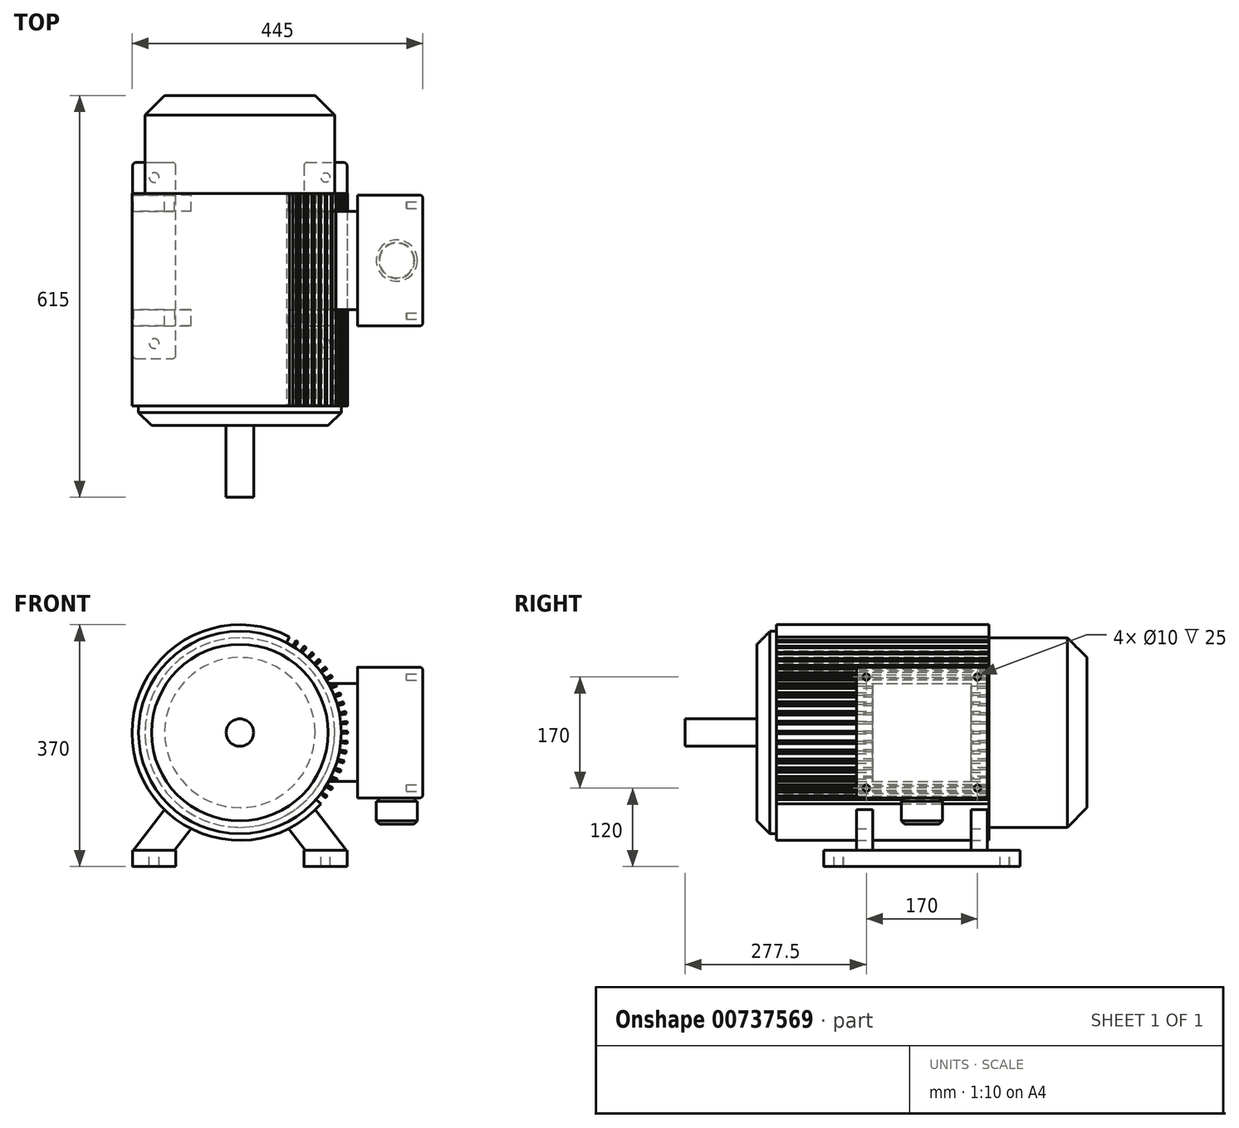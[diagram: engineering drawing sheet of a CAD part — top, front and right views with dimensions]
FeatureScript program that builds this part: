
annotation { "Feature Type Name" : "Feature", "Feature Type Description" : "" }
export const myFeature = defineFeature(function(context is Context, id is Id, definition is map)
    precondition{}
    {
        {
            var Q0;
            Q0=qCreatedBy(makeId("Front.planeOp"),FACE);
            var sketch = newSketch(context, id + "F0", { "sketchPlane" : qUnion([Q0])});
            skCircle(sketch, "E0", {"center": v(0, 0) * mm, "radius": 165 * mm});
            skSolve(sketch);
        }
        {
            var Q0;
            Q0=makeQuery(id+"F0.imprint","IMPRINT",FACE,{"disambiguationData":[TD([[makeQuery(id+"F0.imprint","IMPRINT",EDGE,{"derivedFrom":sQuery(id+"F0.wireOp",EDGE,"E0")}),1.0]])]});
            extrude(context, id + "F1", {"entities" : qUnion([Q0]), "endBound" : BoundingType.SYMMETRIC, "depth" : 505 * mm, "offsetDistance" : 25 * mm});
        }
        {
            var Q0;
            Q0=qCreatedBy(makeId("Right.planeOp"),FACE);
            var sketch = newSketch(context, id + "F2", { "sketchPlane" : qUnion([Q0])});
            skLineSegment(sketch, "E1", {"start": v(-447.5, 165) * mm, "end": v(252.5, 165) * mm});
            skLineSegment(sketch, "E2", {"start": v(252.5, 165) * mm, "end": v(252.5, 115) * mm});
            skLineSegment(sketch, "E3", {"start": v(252.5, 115) * mm, "end": v(202.5, 165) * mm});
            skSolve(sketch);
        }
        {
            var Q0;
            Q0 = qSketchRegion(id + "F2", true);
            var Q1;
            Q1=makeQuery(id+"F1.opExtrude","SWEPT_FACE",FACE,{"disambiguationData":[OSD([sQuery(id+"F0.wireOp",EDGE,"E0")])]});
            revolve(context, id + "F3", {"operationType" : NewBodyOperationType.REMOVE, "surfaceOperationType" : NewSurfaceOperationType.NEW, "entities" : qUnion([Q0]), "axis" : qUnion([Q1]), "revolveType" : RevolveType.FULL, "oppositeDirection" : true});
        }
        {
            var Q0;
            Q0=qCreatedBy(makeId("Right.planeOp"),FACE);
            var sketch = newSketch(context, id + "F4", { "sketchPlane" : qUnion([Q0])});
            skLineSegment(sketch, "E4", {"start": v(-447.5, 165) * mm, "end": v(377.5, 165) * mm});
            skLineSegment(sketch, "E5.bottom", {"start": v(102.5, 165) * mm, "end": v(232.5, 165) * mm});
            skLineSegment(sketch, "E5.top", {"start": v(102.5, 145) * mm, "end": v(232.5, 145) * mm});
            skLineSegment(sketch, "E5.left", {"start": v(102.5, 165) * mm, "end": v(102.5, 145) * mm});
            skLineSegment(sketch, "E5.right", {"start": v(232.5, 165) * mm, "end": v(232.5, 145) * mm});
            skSolve(sketch);
        }
        {
            var Q0;
            Q0 = qSketchRegion(id + "F4", true);
            var Q1;
            Q1=makeQuery(id+"F1.opExtrude","SWEPT_FACE",FACE,{"disambiguationData":[OSD([sQuery(id+"F0.wireOp",EDGE,"E0")])]});
            revolve(context, id + "F5", {"operationType" : NewBodyOperationType.REMOVE, "surfaceOperationType" : NewSurfaceOperationType.NEW, "entities" : qUnion([Q0]), "axis" : qUnion([Q1]), "revolveType" : RevolveType.FULL, "oppositeDirection" : true});
        }
        {
            var Q0;
            Q0=qCreatedBy(makeId("Right.planeOp"),FACE);
            var sketch = newSketch(context, id + "F6", { "sketchPlane" : qUnion([Q0])});
            skLineSegment(sketch, "E6", {"start": v(-447.5, 165) * mm, "end": v(-252.5, 165) * mm});
            skLineSegment(sketch, "E7", {"start": v(-174.48, 165) * mm, "end": v(-174.48, 165) * mm});
            skPoint(sketch, "E8.orphan", {"position": v(-252.5, -165) * mm});
            skLineSegment(sketch, "E9", {"start": v(-252.5, 165) * mm, "end": v(-222.5, 165) * mm});
            skLineSegment(sketch, "E10", {"start": v(-222.5, 165) * mm, "end": v(-222.5, 155) * mm});
            skLineSegment(sketch, "E11", {"start": v(-222.5, 155) * mm, "end": v(-232.5, 155) * mm});
            skLineSegment(sketch, "E12", {"start": v(-232.5, 155) * mm, "end": v(-252.5, 135) * mm});
            skLineSegment(sketch, "E13", {"start": v(-252.5, 135) * mm, "end": v(-252.5, 165) * mm});
            skSolve(sketch);
        }
        {
            var Q0;
            Q0 = qSketchRegion(id + "F6", true);
            var Q1;
            Q1=makeQuery(id+"F1.opExtrude","SWEPT_FACE",FACE,{"disambiguationData":[OSD([sQuery(id+"F0.wireOp",EDGE,"E0")])]});
            revolve(context, id + "F7", {"operationType" : NewBodyOperationType.REMOVE, "surfaceOperationType" : NewSurfaceOperationType.NEW, "entities" : qUnion([Q0]), "axis" : qUnion([Q1]), "revolveType" : RevolveType.FULL, "oppositeDirection" : true});
        }
        {
            var Q0;
            Q0=makeQuery(id+"F7.boolean.opBoolean","COPY",FACE,{"derivedFrom":makeQuery(id+"F7.opRevolve","SWEPT_FACE",FACE,{"disambiguationData":[OSD([sQuery(id+"F6.wireOp",EDGE,"E10")])]})});
            var sketch = newSketch(context, id + "F8", { "sketchPlane" : qUnion([Q0])});
            skLineSegment(sketch, "E14", {"start": v(71.15, 137.7) * mm, "end": v(83.26, 158.68) * mm});
            skLineSegment(sketch, "E15", {"start": v(83.26, 158.68) * mm, "end": v(92.77, 153.19) * mm});
            skLineSegment(sketch, "E16", {"start": v(92.77, 153.19) * mm, "end": v(80.73, 132.32) * mm});
            skLineSegment(sketch, "E17", {"start": v(80.73, 132.32) * mm, "end": v(71.15, 137.7) * mm});
            skLineSegment(sketch, "E18.1.0", {"start": v(106.43, 144.03) * mm, "end": v(92.52, 124.36) * mm});
            skLineSegment(sketch, "E18.1.1", {"start": v(83.49, 130.6) * mm, "end": v(97.47, 150.37) * mm});
            skLineSegment(sketch, "E18.1.2", {"start": v(97.47, 150.37) * mm, "end": v(106.43, 144.03) * mm});
            skLineSegment(sketch, "E18.1.3", {"start": v(92.52, 124.36) * mm, "end": v(83.49, 130.6) * mm});
            skLineSegment(sketch, "E18.2.0", {"start": v(119.2, 133.66) * mm, "end": v(103.54, 115.34) * mm});
            skLineSegment(sketch, "E18.2.1", {"start": v(95.11, 122.39) * mm, "end": v(110.85, 140.8) * mm});
            skLineSegment(sketch, "E18.2.2", {"start": v(110.85, 140.8) * mm, "end": v(119.2, 133.66) * mm});
            skLineSegment(sketch, "E18.2.3", {"start": v(103.54, 115.34) * mm, "end": v(95.11, 122.39) * mm});
            skLineSegment(sketch, "E18.3.0", {"start": v(130.95, 122.16) * mm, "end": v(113.68, 105.36) * mm});
            skLineSegment(sketch, "E18.3.1", {"start": v(105.94, 113.15) * mm, "end": v(123.3, 130.03) * mm});
            skLineSegment(sketch, "E18.3.2", {"start": v(123.3, 130.03) * mm, "end": v(130.95, 122.16) * mm});
            skLineSegment(sketch, "E18.3.3", {"start": v(113.68, 105.36) * mm, "end": v(105.94, 113.15) * mm});
            skLineSegment(sketch, "E18.4.0", {"start": v(141.6, 109.63) * mm, "end": v(122.87, 94.49) * mm});
            skLineSegment(sketch, "E18.4.1", {"start": v(115.87, 102.95) * mm, "end": v(134.7, 118.17) * mm});
            skLineSegment(sketch, "E18.4.2", {"start": v(134.7, 118.17) * mm, "end": v(141.6, 109.63) * mm});
            skLineSegment(sketch, "E18.4.3", {"start": v(122.87, 94.49) * mm, "end": v(115.87, 102.95) * mm});
            skLineSegment(sketch, "E18.5.0", {"start": v(151.07, 96.18) * mm, "end": v(131.02, 82.82) * mm});
            skLineSegment(sketch, "E18.5.1", {"start": v(124.83, 91.89) * mm, "end": v(144.98, 105.32) * mm});
            skLineSegment(sketch, "E18.5.2", {"start": v(144.98, 105.32) * mm, "end": v(151.07, 96.18) * mm});
            skLineSegment(sketch, "E18.5.3", {"start": v(131.02, 82.82) * mm, "end": v(124.83, 91.89) * mm});
            skLineSegment(sketch, "E18.6.0", {"start": v(159.25, 81.92) * mm, "end": v(138.06, 70.45) * mm});
            skLineSegment(sketch, "E18.6.1", {"start": v(132.73, 80.05) * mm, "end": v(154.03, 91.58) * mm});
            skLineSegment(sketch, "E18.6.2", {"start": v(154.03, 91.58) * mm, "end": v(159.25, 81.92) * mm});
            skLineSegment(sketch, "E18.6.3", {"start": v(138.06, 70.45) * mm, "end": v(132.73, 80.05) * mm});
            skLineSegment(sketch, "E18.7.0", {"start": v(166.1, 66.97) * mm, "end": v(143.94, 57.49) * mm});
            skLineSegment(sketch, "E18.7.1", {"start": v(139.51, 67.54) * mm, "end": v(161.78, 77.06) * mm});
            skLineSegment(sketch, "E18.7.2", {"start": v(161.78, 77.06) * mm, "end": v(166.1, 66.97) * mm});
            skLineSegment(sketch, "E18.7.3", {"start": v(143.94, 57.49) * mm, "end": v(139.51, 67.54) * mm});
            skLineSegment(sketch, "E18.8.0", {"start": v(171.54, 51.45) * mm, "end": v(148.61, 44.04) * mm});
            skLineSegment(sketch, "E18.8.1", {"start": v(145.12, 54.46) * mm, "end": v(168.16, 61.9) * mm});
            skLineSegment(sketch, "E18.8.2", {"start": v(168.16, 61.9) * mm, "end": v(171.54, 51.45) * mm});
            skLineSegment(sketch, "E18.8.3", {"start": v(148.61, 44.04) * mm, "end": v(145.12, 54.46) * mm});
            skLineSegment(sketch, "E18.9.0", {"start": v(175.53, 35.5) * mm, "end": v(152.02, 30.23) * mm});
            skLineSegment(sketch, "E18.9.1", {"start": v(149.5, 40.91) * mm, "end": v(173.13, 46.21) * mm});
            skLineSegment(sketch, "E18.9.2", {"start": v(173.13, 46.21) * mm, "end": v(175.53, 35.5) * mm});
            skLineSegment(sketch, "E18.9.3", {"start": v(152.02, 30.23) * mm, "end": v(149.5, 40.91) * mm});
            skLineSegment(sketch, "E18.10.0", {"start": v(178.05, 19.24) * mm, "end": v(154.16, 16.15) * mm});
            skLineSegment(sketch, "E18.10.1", {"start": v(152.63, 27.03) * mm, "end": v(176.64, 30.13) * mm});
            skLineSegment(sketch, "E18.10.2", {"start": v(176.64, 30.13) * mm, "end": v(178.05, 19.24) * mm});
            skLineSegment(sketch, "E18.10.3", {"start": v(154.16, 16.15) * mm, "end": v(152.63, 27.03) * mm});
            skLineSegment(sketch, "E18.11.0", {"start": v(179.07, 2.83) * mm, "end": v(154.99, 1.94) * mm});
            skLineSegment(sketch, "E18.11.1", {"start": v(154.46, 12.91) * mm, "end": v(178.66, 13.8) * mm});
            skLineSegment(sketch, "E18.11.2", {"start": v(178.66, 13.8) * mm, "end": v(179.07, 2.83) * mm});
            skLineSegment(sketch, "E18.11.3", {"start": v(154.99, 1.94) * mm, "end": v(154.46, 12.91) * mm});
            skLineSegment(sketch, "E18.12.0", {"start": v(178.57, -13.6) * mm, "end": v(154.51, -12.28) * mm});
            skLineSegment(sketch, "E18.12.1", {"start": v(155, -1.3) * mm, "end": v(179.17, -2.64) * mm});
            skLineSegment(sketch, "E18.12.2", {"start": v(179.17, -2.64) * mm, "end": v(178.57, -13.6) * mm});
            skLineSegment(sketch, "E18.12.3", {"start": v(154.51, -12.28) * mm, "end": v(155, -1.3) * mm});
            skLineSegment(sketch, "E18.13.0", {"start": v(176.57, -29.93) * mm, "end": v(152.73, -26.4) * mm});
            skLineSegment(sketch, "E18.13.1", {"start": v(154.22, -15.52) * mm, "end": v(178.18, -19.07) * mm});
            skLineSegment(sketch, "E18.13.2", {"start": v(178.18, -19.07) * mm, "end": v(176.57, -29.93) * mm});
            skLineSegment(sketch, "E18.13.3", {"start": v(152.73, -26.4) * mm, "end": v(154.22, -15.52) * mm});
            skLineSegment(sketch, "E18.14.0", {"start": v(173.08, -46) * mm, "end": v(149.67, -40.3) * mm});
            skLineSegment(sketch, "E18.14.1", {"start": v(152.15, -29.6) * mm, "end": v(175.68, -35.33) * mm});
            skLineSegment(sketch, "E18.14.2", {"start": v(175.68, -35.33) * mm, "end": v(173.08, -46) * mm});
            skLineSegment(sketch, "E18.14.3", {"start": v(149.67, -40.3) * mm, "end": v(152.15, -29.6) * mm});
            skLineSegment(sketch, "E18.15.0", {"start": v(168.13, -61.68) * mm, "end": v(145.34, -53.86) * mm});
            skLineSegment(sketch, "E18.15.1", {"start": v(148.79, -43.43) * mm, "end": v(171.7, -51.3) * mm});
            skLineSegment(sketch, "E18.15.2", {"start": v(171.7, -51.3) * mm, "end": v(168.13, -61.68) * mm});
            skLineSegment(sketch, "E18.15.3", {"start": v(145.34, -53.86) * mm, "end": v(148.79, -43.43) * mm});
            skLineSegment(sketch, "E18.16.0", {"start": v(161.76, -76.85) * mm, "end": v(139.79, -66.97) * mm});
            skLineSegment(sketch, "E18.16.1", {"start": v(144.18, -56.9) * mm, "end": v(166.27, -66.83) * mm});
            skLineSegment(sketch, "E18.16.2", {"start": v(166.27, -66.83) * mm, "end": v(161.76, -76.85) * mm});
            skLineSegment(sketch, "E18.16.3", {"start": v(139.79, -66.97) * mm, "end": v(144.18, -56.9) * mm});
            skLineSegment(sketch, "E18.17.0", {"start": v(154.03, -91.36) * mm, "end": v(133.06, -79.5) * mm});
            skLineSegment(sketch, "E18.17.1", {"start": v(138.35, -69.89) * mm, "end": v(159.43, -81.8) * mm});
            skLineSegment(sketch, "E18.17.2", {"start": v(159.43, -81.8) * mm, "end": v(154.03, -91.36) * mm});
            skLineSegment(sketch, "E18.17.3", {"start": v(133.06, -79.5) * mm, "end": v(138.35, -69.89) * mm});
            skLineSegment(sketch, "E18.18.0", {"start": v(145, -105.1) * mm, "end": v(125.2, -91.38) * mm});
            skLineSegment(sketch, "E18.18.1", {"start": v(131.36, -82.28) * mm, "end": v(151.26, -96.08) * mm});
            skLineSegment(sketch, "E18.18.2", {"start": v(151.26, -96.08) * mm, "end": v(145, -105.1) * mm});
            skLineSegment(sketch, "E18.18.3", {"start": v(125.2, -91.38) * mm, "end": v(131.36, -82.28) * mm});
            skLineSegment(sketch, "E18.19.0", {"start": v(134.75, -117.96) * mm, "end": v(116.3, -102.48) * mm});
            skLineSegment(sketch, "E18.19.1", {"start": v(123.26, -93.98) * mm, "end": v(141.8, -109.55) * mm});
            skLineSegment(sketch, "E18.19.2", {"start": v(141.8, -109.55) * mm, "end": v(134.75, -117.96) * mm});
            skLineSegment(sketch, "E18.19.3", {"start": v(116.3, -102.48) * mm, "end": v(123.26, -93.98) * mm});
            skPoint(sketch, "E18.center", {"position": v(0, 0) * mm});
            skLineSegment(sketch, "E18.anchor1", {"start": v(0, 0) * mm, "end": v(71.15, 137.7) * mm, "construction": true});
            skLineSegment(sketch, "E18.anchor2", {"start": v(0, 0) * mm, "end": v(123.26, -93.98) * mm, "construction": true});
            skSolve(sketch);
        }
        {
            var Q0;
            Q0=makeQuery(id+"F1.opExtrude","CAP_FACE",FACE,{"disambiguationData":[OSD([sQuery(id+"F0.wireOp",EDGE,"E0")])],"isStart":false});
            var sketch = newSketch(context, id + "F9", { "sketchPlane" : qUnion([Q0])});
            skCircle(sketch, "E19", {"center": v(0, 0) * mm, "radius": 21 * mm});
            skSolve(sketch);
        }
        {
            var Q0;
            Q0=makeQuery(id+"F9.imprint","IMPRINT",FACE,{"disambiguationData":[TD([[makeQuery(id+"F9.imprint","IMPRINT",EDGE,{"derivedFrom":sQuery(id+"F9.wireOp",EDGE,"E19")}),1.0]])]});
            extrude(context, id + "F10", {"entities" : qUnion([Q0]), "operationType" : NewBodyOperationType.ADD, "depth" : 110 * mm, "offsetDistance" : 25 * mm});
        }
        {
            var Q0;
            Q0=qCreatedBy(makeId("Right.planeOp"),FACE);
            var sketch = newSketch(context, id + "F11", { "sketchPlane" : qUnion([Q0])});
            skLineSegment(sketch, "E20.bottom", {"start": v(75, 75) * mm, "end": v(-75, 75) * mm});
            skLineSegment(sketch, "E20.top", {"start": v(75, -75) * mm, "end": v(-75, -75) * mm});
            skLineSegment(sketch, "E20.left", {"start": v(75, 75) * mm, "end": v(75, -75) * mm});
            skLineSegment(sketch, "E20.right", {"start": v(-75, 75) * mm, "end": v(-75, -75) * mm});
            skPoint(sketch, "E20.middle", {"position": v(0, 0) * mm});
            skSolve(sketch);
        }
        {
            var Q0;
            Q0 = qSketchRegion(id + "F11", true);
            extrude(context, id + "F12", {"entities" : qUnion([Q0]), "operationType" : NewBodyOperationType.ADD, "depth" : 180 * mm, "offsetDistance" : 25 * mm});
        }
        {
            var Q0;
            Q0=makeQuery(id+"F12.opExtrude","CAP_FACE",FACE,{"disambiguationData":[OSD([sQuery(id+"F11.wireOp",EDGE,"E20.bottom"),sQuery(id+"F11.wireOp",EDGE,"E20.top"),sQuery(id+"F11.wireOp",EDGE,"E20.left"),sQuery(id+"F11.wireOp",EDGE,"E20.right")])],"isStart":false});
            var sketch = newSketch(context, id + "F13", { "sketchPlane" : qUnion([Q0])});
            skLineSegment(sketch, "E21.bottom", {"start": v(100, 100) * mm, "end": v(-100, 100) * mm});
            skLineSegment(sketch, "E21.top", {"start": v(100, -100) * mm, "end": v(-100, -100) * mm});
            skLineSegment(sketch, "E21.left", {"start": v(100, 100) * mm, "end": v(100, -100) * mm});
            skLineSegment(sketch, "E21.right", {"start": v(-100, 100) * mm, "end": v(-100, -100) * mm});
            skPoint(sketch, "E21.middle", {"position": v(0, 0) * mm});
            skSolve(sketch);
        }
        {
            var Q0;
            Q0 = qSketchRegion(id + "F13", true);
            extrude(context, id + "F14", {"entities" : qUnion([Q0]), "operationType" : NewBodyOperationType.ADD, "depth" : 100 * mm, "offsetDistance" : 25 * mm});
        }
        {
            var Q0;
            Q0=makeQuery(id+"F14.opExtrude","SWEPT_EDGE",EDGE,{"disambiguationData":[OSD([sQuery(id+"F13.wireOp",EDGE,"E21.bottom"),sQuery(id+"F13.wireOp",EDGE,"E21.right")])]});
            var Q1;
            Q1=makeQuery(id+"F14.opExtrude","CAP_FACE",FACE,{"disambiguationData":[OSD([sQuery(id+"F13.wireOp",EDGE,"E21.bottom"),sQuery(id+"F13.wireOp",EDGE,"E21.top"),sQuery(id+"F13.wireOp",EDGE,"E21.left"),sQuery(id+"F13.wireOp",EDGE,"E21.right")])],"isStart":false});
            var Q2;
            Q2=makeQuery(id+"F14.opExtrude","SWEPT_EDGE",EDGE,{"disambiguationData":[OSD([sQuery(id+"F13.wireOp",EDGE,"E21.bottom"),sQuery(id+"F13.wireOp",EDGE,"E21.left")])]});
            var Q3;
            Q3=makeQuery(id+"F14.opExtrude","SWEPT_EDGE",EDGE,{"disambiguationData":[OSD([sQuery(id+"F13.wireOp",EDGE,"E21.top"),sQuery(id+"F13.wireOp",EDGE,"E21.left")])]});
            var Q4;
            Q4=makeQuery(id+"F14.opExtrude","SWEPT_EDGE",EDGE,{"disambiguationData":[OSD([sQuery(id+"F13.wireOp",EDGE,"E21.top"),sQuery(id+"F13.wireOp",EDGE,"E21.right")])]});
            fillet(context, id + "F15", {"entities" : qUnion([Q0, Q1, Q2, Q3, Q4]), "radius" : 5 * mm, "tangentPropagation" : true, "allowEdgeOverflow" : false});
        }
        {
            var Q0;
            Q0=makeQuery(id+"F14.opExtrude","CAP_FACE",FACE,{"disambiguationData":[OSD([sQuery(id+"F13.wireOp",EDGE,"E21.bottom"),sQuery(id+"F13.wireOp",EDGE,"E21.top"),sQuery(id+"F13.wireOp",EDGE,"E21.left"),sQuery(id+"F13.wireOp",EDGE,"E21.right")])],"isStart":false});
            var sketch = newSketch(context, id + "F16", { "sketchPlane" : qUnion([Q0])});
            skCircle(sketch, "E22", {"center": v(-85, 85) * mm, "radius": 5 * mm});
            skCircle(sketch, "E23.0.1.0", {"center": v(-85, -85) * mm, "radius": 5 * mm});
            skCircle(sketch, "E23.1.0.0", {"center": v(85, 85) * mm, "radius": 5 * mm});
            skCircle(sketch, "E23.1.1.0", {"center": v(85, -85) * mm, "radius": 5 * mm});
            skLineSegment(sketch, "E23.direction1", {"start": v(-85, 85) * mm, "end": v(85, 85) * mm, "construction": true});
            skLineSegment(sketch, "E23.direction2", {"start": v(-85, 85) * mm, "end": v(-85, -85) * mm, "construction": true});
            skSolve(sketch);
        }
        {
            var Q0;
            Q0 = qSketchRegion(id + "F16", true);
            extrude(context, id + "F17", {"entities" : qUnion([Q0]), "operationType" : NewBodyOperationType.REMOVE, "oppositeDirection" : true, "depth" : 25 * mm, "offsetDistance" : 25 * mm});
        }
        {
            var Q0;
            Q0=makeQuery(id+"F14.opExtrude","SWEPT_FACE",FACE,{"disambiguationData":[OSD([sQuery(id+"F13.wireOp",EDGE,"E21.right")])]});
            var sketch = newSketch(context, id + "F18", { "sketchPlane" : qUnion([Q0])});
            skLineSegment(sketch, "E24", {"start": v(-43.84, 91.73) * mm, "end": v(-38.95, 85.3) * mm});
            skLineSegment(sketch, "E25", {"start": v(162.82, -180) * mm, "end": v(100, -180) * mm});
            skLineSegment(sketch, "E26", {"start": v(-83, 60.62) * mm, "end": v(-43.2, 90.9) * mm});
            skLineSegment(sketch, "E27.trimOffspring", {"start": v(-83, 60.62) * mm, "end": v(100, -180) * mm});
            skLineSegment(sketch, "E28.trimOffspring", {"start": v(-43.2, 90.9) * mm, "end": v(162.82, -180) * mm});
            skPoint(sketch, "E29.0.center.orphan", {"position": v(0, 0) * mm});
            skLineSegment(sketch, "E30.MirrorCS", {"start": v(43.84, 91.73) * mm, "end": v(38.95, 85.3) * mm});
            skLineSegment(sketch, "E31.MirrorCS", {"start": v(83, 60.62) * mm, "end": v(43.2, 90.9) * mm});
            skLineSegment(sketch, "E32.MirrorCS", {"start": v(43.2, 90.9) * mm, "end": v(-162.82, -180) * mm});
            skLineSegment(sketch, "E33.MirrorCS", {"start": v(-162.82, -180) * mm, "end": v(-100, -180) * mm});
            skLineSegment(sketch, "E34.MirrorCS", {"start": v(83, 60.62) * mm, "end": v(-100, -180) * mm});
            skSolve(sketch);
        }
        {
            var Q0;
            Q0 = qSketchRegion(id + "F18", true);
            extrude(context, id + "F19", {"entities" : qUnion([Q0]), "operationType" : NewBodyOperationType.ADD, "oppositeDirection" : true, "depth" : 25 * mm, "offsetDistance" : 25 * mm});
        }
        {
            var Q0;
            Q0=makeQuery(id+"F14.opExtrude","SWEPT_FACE",FACE,{"disambiguationData":[OSD([sQuery(id+"F13.wireOp",EDGE,"E21.left")])]});
            var sketch = newSketch(context, id + "F20", { "sketchPlane" : qUnion([Q0])});
            skLineSegment(sketch, "E35.0", {"start": v(43.2, 90.9) * mm, "end": v(-162.82, -180) * mm});
            skLineSegment(sketch, "E36.0", {"start": v(83, 60.62) * mm, "end": v(-100, -180) * mm});
            skLineSegment(sketch, "E37.0", {"start": v(83, 60.62) * mm, "end": v(43.2, 90.9) * mm});
            skLineSegment(sketch, "E38.0", {"start": v(-162.82, -180) * mm, "end": v(-100, -180) * mm});
            skLineSegment(sketch, "E39.0", {"start": v(-83, 60.62) * mm, "end": v(-43.2, 90.9) * mm});
            skLineSegment(sketch, "E40.0", {"start": v(-43.2, 90.9) * mm, "end": v(162.82, -180) * mm});
            skLineSegment(sketch, "E41.0", {"start": v(-83, 60.62) * mm, "end": v(100, -180) * mm});
            skLineSegment(sketch, "E42.0", {"start": v(162.82, -180) * mm, "end": v(100, -180) * mm});
            skSolve(sketch);
        }
        {
            var Q0;
            Q0 = qSketchRegion(id + "F20", true);
            extrude(context, id + "F21", {"entities" : qUnion([Q0]), "operationType" : NewBodyOperationType.ADD, "oppositeDirection" : true, "depth" : 25 * mm, "offsetDistance" : 25 * mm});
        }
        {
            var Q0;
            Q0=makeQuery(id+"F19.opExtrude","SWEPT_FACE",FACE,{"disambiguationData":[OSD([sQuery(id+"F18.wireOp",EDGE,"E33.MirrorCS")])]});
            var sketch = newSketch(context, id + "F22", { "sketchPlane" : qUnion([Q0])});
            skLineSegment(sketch, "E43.bottom", {"start": v(-164, 150) * mm, "end": v(-98, 150) * mm});
            skLineSegment(sketch, "E43.top", {"start": v(-164, -150) * mm, "end": v(-98, -150) * mm});
            skLineSegment(sketch, "E43.left", {"start": v(-164, 150) * mm, "end": v(-164, -150) * mm});
            skLineSegment(sketch, "E43.right", {"start": v(-98, 150) * mm, "end": v(-98, -150) * mm});
            skCircle(sketch, "E44", {"center": v(-131, 127) * mm, "radius": 7.5 * mm});
            skCircle(sketch, "E45.MirrorC", {"center": v(-131, -127) * mm, "radius": 7.5 * mm});
            skLineSegment(sketch, "E46.MirrorCS", {"start": v(-164, 150) * mm, "end": v(-164, 450) * mm});
            skLineSegment(sketch, "E47.MirrorCS", {"start": v(-98, 150) * mm, "end": v(-98, 450) * mm});
            skSolve(sketch);
        }
        {
            var Q0;
            Q0 = qSketchRegion(id + "F22", true);
            extrude(context, id + "F23", {"entities" : qUnion([Q0]), "operationType" : NewBodyOperationType.ADD, "depth" : 25 * mm, "offsetDistance" : 25 * mm});
        }
        {
            var Q0;
            Q0=makeQuery(id+"F23.opExtrude","SWEPT_EDGE",EDGE,{"disambiguationData":[OSD([sQuery(id+"F22.wireOp",EDGE,"E43.bottom"),sQuery(id+"F22.wireOp",EDGE,"E43.left")])]});
            var Q1;
            Q1=makeQuery(id+"F23.opExtrude","SWEPT_EDGE",EDGE,{"disambiguationData":[OSD([sQuery(id+"F22.wireOp",EDGE,"E43.bottom"),sQuery(id+"F22.wireOp",EDGE,"E43.right")])]});
            var Q2;
            Q2=makeQuery(id+"F23.opExtrude","SWEPT_EDGE",EDGE,{"disambiguationData":[OSD([sQuery(id+"F22.wireOp",EDGE,"E43.top"),sQuery(id+"F22.wireOp",EDGE,"E43.right")])]});
            var Q3;
            Q3=makeQuery(id+"F23.opExtrude","SWEPT_EDGE",EDGE,{"disambiguationData":[OSD([sQuery(id+"F22.wireOp",EDGE,"E43.top"),sQuery(id+"F22.wireOp",EDGE,"E43.left")])]});
            fillet(context, id + "F24", {"entities" : qUnion([Q0, Q1, Q2, Q3]), "radius" : 5 * mm, "tangentPropagation" : true, "allowEdgeOverflow" : false});
        }
        {
            var Q0;
            Q0=makeQuery(id+"F14.opExtrude","SWEPT_FACE",FACE,{"disambiguationData":[OSD([sQuery(id+"F13.wireOp",EDGE,"E21.top")])]});
            var sketch = newSketch(context, id + "F25", { "sketchPlane" : qUnion([Q0])});
            skCircle(sketch, "E48", {"center": v(240, 0) * mm, "radius": 27.5 * mm});
            skSolve(sketch);
        }
        {
            var Q0;
            Q0=makeQuery(id+"F25.imprint","IMPRINT",FACE,{"disambiguationData":[TD([[makeQuery(id+"F25.imprint","IMPRINT",EDGE,{"derivedFrom":sQuery(id+"F25.wireOp",EDGE,"E48")}),1.0]])]});
            extrude(context, id + "F26", {"entities" : qUnion([Q0]), "operationType" : NewBodyOperationType.ADD, "depth" : 5 * mm, "offsetDistance" : 25 * mm});
        }
        {
            var Q0;
            Q0=makeQuery(id+"F26.opExtrude","CAP_FACE",FACE,{"disambiguationData":[OSD([sQuery(id+"F25.wireOp",EDGE,"E48")])],"isStart":false});
            var sketch = newSketch(context, id + "F27", { "sketchPlane" : qUnion([Q0])});
            skCircle(sketch, "E49", {"center": v(240, 0) * mm, "radius": 31.5 * mm});
            skSolve(sketch);
        }
        {
            var Q0;
            Q0 = qSketchRegion(id + "F27", true);
            extrude(context, id + "F28", {"entities" : qUnion([Q0]), "operationType" : NewBodyOperationType.ADD, "depth" : 35 * mm, "offsetDistance" : 25 * mm});
        }
        {
            var Q0;
            Q0=makeQuery(id+"F28.opExtrude","CAP_EDGE",EDGE,{"disambiguationData":[OSD([sQuery(id+"F27.wireOp",EDGE,"E49")])],"isStart":false});
            chamfer(context, id + "F29", {"entities" : qUnion([Q0]), "width" : 5 * mm, "tangentPropagation" : true});
        }
        {
            var Q0;
            Q0=makeQuery(id+"F19.opExtrude","SWEPT_FACE",FACE,{"disambiguationData":[OSD([sQuery(id+"F18.wireOp",EDGE,"E25")])]});
            var sketch = newSketch(context, id + "F30", { "sketchPlane" : qUnion([Q0])});
            skLineSegment(sketch, "E50.bottom", {"start": v(98, -150) * mm, "end": v(164, -150) * mm});
            skLineSegment(sketch, "E50.top", {"start": v(98, 150) * mm, "end": v(164, 150) * mm});
            skLineSegment(sketch, "E50.left", {"start": v(98, -150) * mm, "end": v(98, 150) * mm});
            skLineSegment(sketch, "E50.right", {"start": v(164, -150) * mm, "end": v(164, 150) * mm});
            skPoint(sketch, "E50.middle", {"position": v(131, 0) * mm});
            skCircle(sketch, "E51", {"center": v(131, 127) * mm, "radius": 7 * mm});
            skCircle(sketch, "E52.MirrorC", {"center": v(131, -127) * mm, "radius": 7 * mm});
            skSolve(sketch);
        }
        {
            var Q0;
            Q0=makeQuery(id+"F30.imprint","IMPRINT",FACE,{"disambiguationData":[TD([[makeQuery(id+"F30.imprint","IMPRINT",EDGE,{"derivedFrom":sQuery(id+"F30.wireOp",EDGE,"E50.bottom")}),1.0]])]});
            var Q1;
            {var subQ0=sQuery(id+"F18.wireOp",EDGE,"E25");Q1=makeQuery(id+"F30.imprint","IMPRINT",FACE,{"disambiguationData":[TD([[makeQuery(id+"F30.imprint","IMPRINT",EDGE,{"derivedFrom":makeQuery(id+"F19.opExtrude","CAP_EDGE",EDGE,{"disambiguationData":[OSD([subQ0])],"isStart":true})}),1.0]])]});}
            extrude(context, id + "F31", {"entities" : qUnion([Q0, Q1]), "operationType" : NewBodyOperationType.ADD, "depth" : 25 * mm, "offsetDistance" : 25 * mm});
        }
        {
            var Q0;
            Q0=makeQuery(id+"F31.opExtrude","SWEPT_EDGE",EDGE,{"disambiguationData":[OSD([sQuery(id+"F30.wireOp",EDGE,"E50.top"),sQuery(id+"F30.wireOp",EDGE,"E50.right")])]});
            var Q1;
            Q1=makeQuery(id+"F31.opExtrude","SWEPT_EDGE",EDGE,{"disambiguationData":[OSD([sQuery(id+"F30.wireOp",EDGE,"E50.top"),sQuery(id+"F30.wireOp",EDGE,"E50.left")])]});
            var Q2;
            Q2=makeQuery(id+"F31.opExtrude","SWEPT_EDGE",EDGE,{"disambiguationData":[OSD([sQuery(id+"F30.wireOp",EDGE,"E50.bottom"),sQuery(id+"F30.wireOp",EDGE,"E50.right")])]});
            var Q3;
            Q3=makeQuery(id+"F31.opExtrude","SWEPT_EDGE",EDGE,{"disambiguationData":[OSD([sQuery(id+"F30.wireOp",EDGE,"E50.bottom"),sQuery(id+"F30.wireOp",EDGE,"E50.left")])]});
            fillet(context, id + "F32", {"entities" : qUnion([Q0, Q1, Q2, Q3]), "radius" : 5 * mm, "tangentPropagation" : true, "allowEdgeOverflow" : false});
        }
        {
            var Q0;
            Q0 = qSketchRegion(id + "F8", true);
            extrude(context, id + "F33", {"entities" : qUnion([Q0]), "operationType" : NewBodyOperationType.REMOVE, "endBound" : BoundingType.THROUGH_ALL, "oppositeDirection" : true, "depth" : 25 * mm, "offsetDistance" : 25 * mm});
        }
        {
            var Q0;
            Q0 = qSketchRegion(id + "F11", true);
            extrude(context, id + "F34", {"entities" : qUnion([Q0]), "operationType" : NewBodyOperationType.ADD, "depth" : 200 * mm, "offsetDistance" : 25 * mm});
        }
    });
